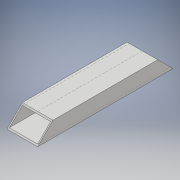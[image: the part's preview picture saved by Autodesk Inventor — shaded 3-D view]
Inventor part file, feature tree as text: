
AUTODESK INVENTOR PART (.ipt)
format: ipt  version: 2018 (Build 220112000, 112)  size: 103,936 bytes
history: native  units: mm
features: other x1, extrude x1, chamfer x1, sketch x1
ambient origin geometry x8: Origin, YZ Plane, XZ Plane, XY Plane, X Axis, Y Axis, Z Axis, Center Point
bodies: Body1 (feature_tree)
feature tree (4):
  other  "ソリッド1"
  extrude  "押し出し1"  Depth=60.0mm
  chamfer  "面取り1"  Distance=30.0mm
  sketch  "スケッチ1"
